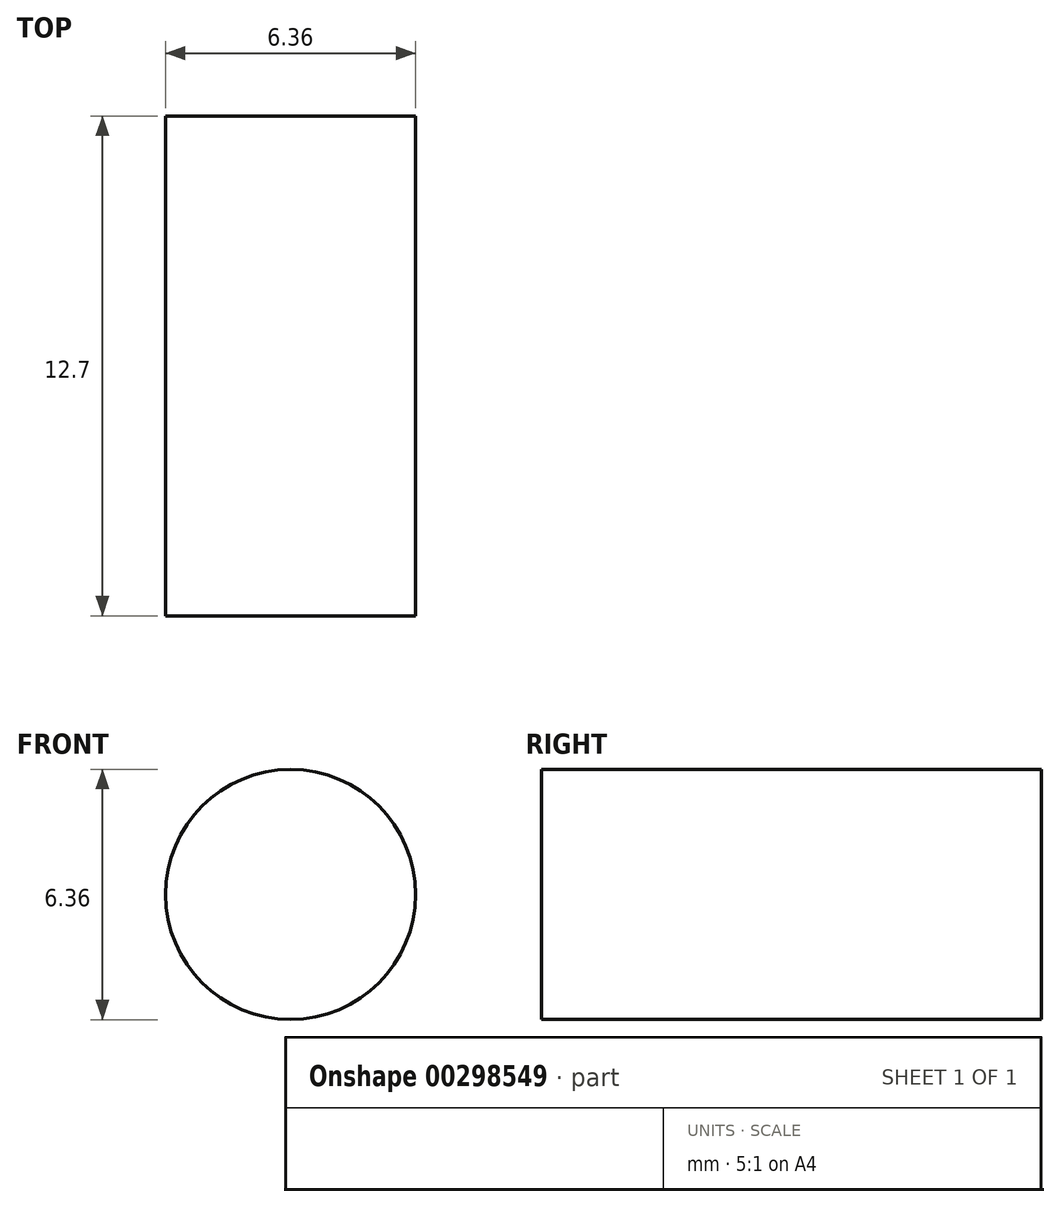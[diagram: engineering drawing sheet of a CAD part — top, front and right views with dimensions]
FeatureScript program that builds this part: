
annotation { "Feature Type Name" : "Feature", "Feature Type Description" : "" }
export const myFeature = defineFeature(function(context is Context, id is Id, definition is map)
    precondition{}
    {
        {
            var Q0;
            Q0=qCreatedBy(makeId("Front.planeOp"),FACE);
            var sketch = newSketch(context, id + "F0", { "sketchPlane" : qUnion([Q0])});
            skCircle(sketch, "E0", {"center": v(0, 0) * mm, "radius": 3.18 * mm});
            skSolve(sketch);
        }
        {
            var Q0;
            Q0=qSketchRegion(id+"F0",true);
            extrude(context, id + "F1", {"entities" : qUnion([Q0]), "depth" : 12.7 * mm});
        }
    });
